# Revit family: ShowerHeadConnectionPipe-90Degree-WallMounted-Vitra-ShowerSystem-A42631
name_source: partatom
category: Plumbing Fixtures
revit_build: Autodesk Revit 2017 (Build: 20160225_1515(x64)
units: mm (PartAtom-declared; Revit-internal decimal feet)

## family parameters
Cut with Voids When Loaded = No
Host = Face
OmniClass Number = 23.45.00.00
OmniClass Title = Sanitary, Laundry, and Cleaning Equipment
Part Type = Normal
Room Calculation Point = No
Round Connector Dimension = Use Diameter
Shared = Yes

## types (5) — shared parameters
BIMobject category = Bath/Shower Mixer
Brand = Vitra
CW Connection = Yes
Connection Diameter (mm) = 15 mm  [stored 0.0492126 ft]
Default Elevation = 2200 mm
Description = Connection Pipe  -  90 Degree-wall mounted
Design country = Turkey
HW Connection = Yes
Hot Water Supply (max.) = 80 °C
Hot Water temperature, factory set to = 38 °C
IFC Classification = Sanitary Terminal
Main Material = Metal
Manufacturer = Vitra
Manufacturer name = Vitra
Masterformat 2014 Code = 22 41 23
Masterformat 2014 Description = Residential Showers
Min. flow pressure of = 0.5 bar
Mounting type = Wall-Mounted Connection Pipe
NBS Referans Code = 35-06-81
NBS Referans Description = Shower Heads
Nominal Depth (mm) = 345 mm  [stored 1.13189 ft]
Nominal Height (mm) = 90 mm
Nominal Width (mm) = 60 mm  [stored 0.19685 ft]
Number Of Connections = 1
OmniClass Code = 23-31 17 19
OmniClass Description = Shower Head Fixtures
Product Type = Shower Connection Pipes
Product certification = https://www.vitraglobal.com
Product family = Shower System
Product group = Wall-Mounted Connection Pipe
Product url = https://www.vitraglobal.com
Range of Hot Water Supply = 5 - 65 °C
Range of flow pressure = 0.5-10 bar (Recommended 3-5 Bars)
Technical description = https://www.vitraglobal.com
Test Pressure = 16 bar
URL = https://vitraglobal.com
Uniclass 1.4 Code = L7214
Uniclass 1.4 Description = Showers
Uniclass 2.0 Code = PR-35-06-81
Uniclass 2.0 Description = Shower Heads
Uniclass 2015 Code = Pr_40_20_87_76
Uniclass 2015 Name = Shower heads
Uniformat II Code = D2010
Uniformat II Description = Plumbing Fixtures
Vent Connection = No
Warranty Period (Year) = 5 Years
Waste Connection = No
Weight Net (kg) = 0.48
Youtube = https://www.youtube.com

## per-type parameters (varying)
| type | Article No. (default) | Coating Material | Color | Model | Product SKU |
| ShowerHeadConnectionPipe-90Degree-WallMounted-Vitra-ShowerSystem-A42631 | A42631 | Chrome | Chrome | A42631 | A42631 |
| ShowerHeadConnectionPipe-90Degree-WallMounted-Vitra-ShowerSystem-A4263123 | A4263123 | Gold | Gold | A4263123 | A4263123 |
| ShowerHeadConnectionPipe-90Degree-WallMounted-Vitra-ShowerSystem-A4263136 | A4263136 | Matte Black | Matte Black | A4263136 | A4263136 |
| ShowerHeadConnectionPipe-90Degree-WallMounted-Vitra-ShowerSystem-A4263126 | A4263126 | Copper | Copper | A4263126 | A4263126 |
| ShowerHeadConnectionPipe-90Degree-WallMounted-Vitra-ShowerSystem-A4263134 | A4263134 | Brushed Nickel | Brushed Nickel | A4263134 | A4263134 |

note: [stored X ft] marks values corroborated as IEEE doubles in the binary element streams (Revit-internal decimal feet)

## geometry (parser evidence)
native form markers: Sweep x2
no freeform markers — native parametric forms only
